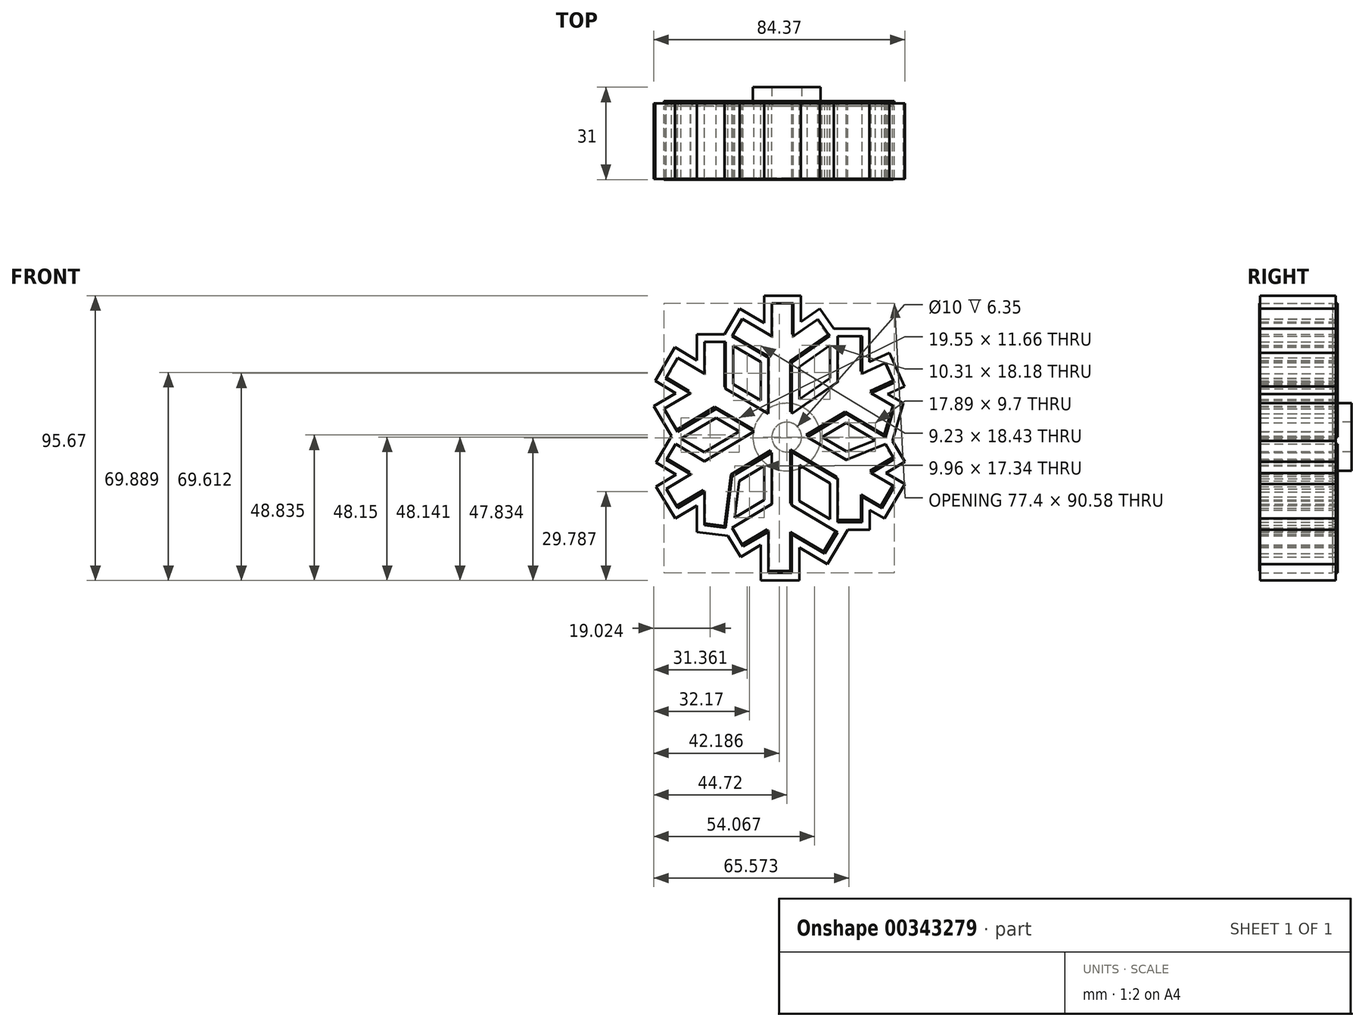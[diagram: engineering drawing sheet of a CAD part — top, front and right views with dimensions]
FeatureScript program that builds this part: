
annotation { "Feature Type Name" : "Feature", "Feature Type Description" : "" }
export const myFeature = defineFeature(function(context is Context, id is Id, definition is map)
    precondition{}
    {
        {
            var Q0;
            Q0=qCreatedBy(makeId("Front.planeOp"),FACE);
            var sketch = newSketch(context, id + "F0", { "sketchPlane" : qUnion([Q0])});
            skLineSegment(sketch, "E0", {"start": v(-40.72, 19.73) * mm, "end": v(-36.61, 26.67) * mm});
            skLineSegment(sketch, "E1", {"start": v(-36.61, 26.67) * mm, "end": v(-27.63, 21.36) * mm});
            skLineSegment(sketch, "E2", {"start": v(-27.63, 21.36) * mm, "end": v(-27.63, 32.04) * mm});
            skLineSegment(sketch, "E3", {"start": v(-27.63, 32.04) * mm, "end": v(-20.52, 32.04) * mm});
            skLineSegment(sketch, "E4", {"start": v(-20.52, 32.04) * mm, "end": v(-20.52, 16.25) * mm});
            skLineSegment(sketch, "E5", {"start": v(-20.52, 16.25) * mm, "end": v(-6.2, 7.8) * mm});
            skLineSegment(sketch, "E6", {"start": v(-6.2, 7.8) * mm, "end": v(-6.2, 21.36) * mm});
            skLineSegment(sketch, "E7", {"start": v(-6.2, 21.36) * mm, "end": v(-6.2, 26.67) * mm});
            skLineSegment(sketch, "E8", {"start": v(-6.2, 26.67) * mm, "end": v(-18.4, 33.87) * mm});
            skLineSegment(sketch, "E9", {"start": v(-18.4, 33.87) * mm, "end": v(-14.94, 39.73) * mm});
            skLineSegment(sketch, "E10", {"start": v(-14.94, 39.73) * mm, "end": v(-5.03, 33.87) * mm});
            skLineSegment(sketch, "E11", {"start": v(-5.03, 33.87) * mm, "end": v(-5.03, 44.98) * mm});
            skLineSegment(sketch, "E12", {"start": v(-5.03, 44.98) * mm, "end": v(2.2, 44.98) * mm});
            skLineSegment(sketch, "E13", {"start": v(2.2, 44.98) * mm, "end": v(2.2, 33.87) * mm});
            skLineSegment(sketch, "E14", {"start": v(2.2, 33.87) * mm, "end": v(10.42, 39.61) * mm});
            skLineSegment(sketch, "E15", {"start": v(10.42, 39.61) * mm, "end": v(14.42, 33.87) * mm});
            skLineSegment(sketch, "E16", {"start": v(14.42, 33.87) * mm, "end": v(1.65, 24.95) * mm});
            skLineSegment(sketch, "E17", {"start": v(1.65, 24.95) * mm, "end": v(1.65, 7.8) * mm});
            skLineSegment(sketch, "E18", {"start": v(1.65, 7.8) * mm, "end": v(17.04, 18.46) * mm});
            skLineSegment(sketch, "E19", {"start": v(17.04, 18.46) * mm, "end": v(17.04, 33.87) * mm});
            skLineSegment(sketch, "E20", {"start": v(17.04, 33.87) * mm, "end": v(25.25, 33.87) * mm});
            skLineSegment(sketch, "E21", {"start": v(25.25, 33.87) * mm, "end": v(25.25, 21.36) * mm});
            skLineSegment(sketch, "E22", {"start": v(25.25, 21.36) * mm, "end": v(33.14, 24.95) * mm});
            skLineSegment(sketch, "E23", {"start": v(33.14, 24.95) * mm, "end": v(36.17, 18.29) * mm});
            skLineSegment(sketch, "E24", {"start": v(36.17, 18.29) * mm, "end": v(28.4, 14.76) * mm});
            skLineSegment(sketch, "E25", {"start": v(28.4, 14.76) * mm, "end": v(36.17, 10.17) * mm});
            skLineSegment(sketch, "E26", {"start": v(36.17, 10.17) * mm, "end": v(33.14, 0) * mm});
            skLineSegment(sketch, "E27", {"start": v(33.14, 0) * mm, "end": v(19.95, 7.8) * mm});
            skLineSegment(sketch, "E28", {"start": v(19.95, 7.8) * mm, "end": v(6.94, 0) * mm});
            skLineSegment(sketch, "E29", {"start": v(6.94, 0) * mm, "end": v(19.95, -7.68) * mm});
            skLineSegment(sketch, "E30", {"start": v(19.95, -7.68) * mm, "end": v(33.14, -2.37) * mm});
            skLineSegment(sketch, "E31", {"start": v(33.14, -2.37) * mm, "end": v(36.17, -7.41) * mm});
            skLineSegment(sketch, "E32", {"start": v(36.17, -7.41) * mm, "end": v(28.4, -12.07) * mm});
            skLineSegment(sketch, "E33", {"start": v(28.4, -12.07) * mm, "end": v(36.17, -16.66) * mm});
            skLineSegment(sketch, "E34", {"start": v(36.17, -16.66) * mm, "end": v(31.88, -23.9) * mm});
            skLineSegment(sketch, "E35", {"start": v(31.88, -23.9) * mm, "end": v(25.32, -20.02) * mm});
            skLineSegment(sketch, "E36", {"start": v(25.32, -20.02) * mm, "end": v(25.32, -28.56) * mm});
            skLineSegment(sketch, "E37", {"start": v(25.32, -28.56) * mm, "end": v(17.04, -28.56) * mm});
            skLineSegment(sketch, "E38", {"start": v(17.04, -28.56) * mm, "end": v(17.04, -14.05) * mm});
            skLineSegment(sketch, "E39", {"start": v(17.04, -14.05) * mm, "end": v(1.65, -4.95) * mm});
            skLineSegment(sketch, "E40", {"start": v(1.65, -4.95) * mm, "end": v(1.65, -22.88) * mm});
            skLineSegment(sketch, "E41", {"start": v(1.65, -22.88) * mm, "end": v(17.04, -31.98) * mm});
            skLineSegment(sketch, "E42", {"start": v(17.04, -31.98) * mm, "end": v(12.78, -39.19) * mm});
            skLineSegment(sketch, "E43", {"start": v(12.78, -39.19) * mm, "end": v(1.65, -32.6) * mm});
            skLineSegment(sketch, "E44", {"start": v(1.65, -32.6) * mm, "end": v(1.65, -45.6) * mm});
            skLineSegment(sketch, "E45", {"start": v(1.65, -45.6) * mm, "end": v(-6.2, -45.6) * mm});
            skLineSegment(sketch, "E46", {"start": v(-6.2, -45.6) * mm, "end": v(-6.2, -31.72) * mm});
            skLineSegment(sketch, "E47", {"start": v(-6.2, -31.72) * mm, "end": v(-14.64, -36.78) * mm});
            skLineSegment(sketch, "E48", {"start": v(-14.64, -36.78) * mm, "end": v(-18.4, -30.51) * mm});
            skLineSegment(sketch, "E49", {"start": v(-18.4, -30.51) * mm, "end": v(-5.03, -22.5) * mm});
            skLineSegment(sketch, "E50", {"start": v(-5.03, -22.5) * mm, "end": v(-5.03, -5.2) * mm});
            skLineSegment(sketch, "E51", {"start": v(-5.03, -5.2) * mm, "end": v(-18.4, -13.22) * mm});
            skLineSegment(sketch, "E52", {"start": v(-18.4, -13.22) * mm, "end": v(-20.52, -30.51) * mm});
            skLineSegment(sketch, "E53", {"start": v(-20.52, -30.51) * mm, "end": v(-27.63, -29.64) * mm});
            skLineSegment(sketch, "E54", {"start": v(-27.63, -29.64) * mm, "end": v(-27.63, -18.46) * mm});
            skLineSegment(sketch, "E55", {"start": v(-27.63, -18.46) * mm, "end": v(-36.61, -23.85) * mm});
            skLineSegment(sketch, "E56", {"start": v(-36.61, -23.85) * mm, "end": v(-40.44, -17.48) * mm});
            skLineSegment(sketch, "E57", {"start": v(-40.44, -17.48) * mm, "end": v(-32.16, -12.52) * mm});
            skLineSegment(sketch, "E58", {"start": v(-32.16, -12.52) * mm, "end": v(-40.44, -7.63) * mm});
            skLineSegment(sketch, "E59", {"start": v(-40.44, -7.63) * mm, "end": v(-37.33, -2.37) * mm});
            skLineSegment(sketch, "E60", {"start": v(-37.33, -2.37) * mm, "end": v(-27.63, -8.1) * mm});
            skLineSegment(sketch, "E61", {"start": v(-27.63, -8.1) * mm, "end": v(-10.95, 1.9) * mm});
            skLineSegment(sketch, "E62", {"start": v(-10.95, 1.9) * mm, "end": v(-20.94, 7.8) * mm});
            skLineSegment(sketch, "E63", {"start": v(-20.94, 7.8) * mm, "end": v(-23.76, 9.47) * mm});
            skLineSegment(sketch, "E64", {"start": v(-23.76, 9.47) * mm, "end": v(-36.61, 1.76) * mm});
            skLineSegment(sketch, "E65", {"start": v(-36.61, 1.76) * mm, "end": v(-41.23, 9.47) * mm});
            skLineSegment(sketch, "E66", {"start": v(-41.23, 9.47) * mm, "end": v(-32.4, 14.76) * mm});
            skLineSegment(sketch, "E67", {"start": v(-32.4, 14.76) * mm, "end": v(-40.72, 19.73) * mm});
            skSolve(sketch);
        }
        {
            var Q0;
            Q0 = qSketchRegion(id + "F0", true);
            extrude(context, id + "F1", {"entities" : qUnion([Q0]), "depth" : .75 * mm});
        }
        {
            var Q0;
            Q0=makeQuery(id+"F1.opExtrude","CAP_FACE",FACE,{"disambiguationData":[OSD([sQuery(id+"F0.wireOp",EDGE,"E0"),sQuery(id+"F0.wireOp",EDGE,"E1"),sQuery(id+"F0.wireOp",EDGE,"E2"),sQuery(id+"F0.wireOp",EDGE,"E3"),sQuery(id+"F0.wireOp",EDGE,"E4"),sQuery(id+"F0.wireOp",EDGE,"E5"),sQuery(id+"F0.wireOp",EDGE,"E6"),sQuery(id+"F0.wireOp",EDGE,"E7"),sQuery(id+"F0.wireOp",EDGE,"E8"),sQuery(id+"F0.wireOp",EDGE,"E9"),sQuery(id+"F0.wireOp",EDGE,"E10"),sQuery(id+"F0.wireOp",EDGE,"E11"),sQuery(id+"F0.wireOp",EDGE,"E12"),sQuery(id+"F0.wireOp",EDGE,"E13"),sQuery(id+"F0.wireOp",EDGE,"E14"),sQuery(id+"F0.wireOp",EDGE,"E15"),sQuery(id+"F0.wireOp",EDGE,"E16"),sQuery(id+"F0.wireOp",EDGE,"E17"),sQuery(id+"F0.wireOp",EDGE,"E18"),sQuery(id+"F0.wireOp",EDGE,"E19"),sQuery(id+"F0.wireOp",EDGE,"E20"),sQuery(id+"F0.wireOp",EDGE,"E21"),sQuery(id+"F0.wireOp",EDGE,"E22"),sQuery(id+"F0.wireOp",EDGE,"E23"),sQuery(id+"F0.wireOp",EDGE,"E24"),sQuery(id+"F0.wireOp",EDGE,"E25"),sQuery(id+"F0.wireOp",EDGE,"E26"),sQuery(id+"F0.wireOp",EDGE,"E27"),sQuery(id+"F0.wireOp",EDGE,"E28"),sQuery(id+"F0.wireOp",EDGE,"E29"),sQuery(id+"F0.wireOp",EDGE,"E30"),sQuery(id+"F0.wireOp",EDGE,"E31"),sQuery(id+"F0.wireOp",EDGE,"E32"),sQuery(id+"F0.wireOp",EDGE,"E33"),sQuery(id+"F0.wireOp",EDGE,"E34"),sQuery(id+"F0.wireOp",EDGE,"E35"),sQuery(id+"F0.wireOp",EDGE,"E36"),sQuery(id+"F0.wireOp",EDGE,"E37"),sQuery(id+"F0.wireOp",EDGE,"E38"),sQuery(id+"F0.wireOp",EDGE,"E39"),sQuery(id+"F0.wireOp",EDGE,"E40"),sQuery(id+"F0.wireOp",EDGE,"E41"),sQuery(id+"F0.wireOp",EDGE,"E42"),sQuery(id+"F0.wireOp",EDGE,"E43"),sQuery(id+"F0.wireOp",EDGE,"E44"),sQuery(id+"F0.wireOp",EDGE,"E45"),sQuery(id+"F0.wireOp",EDGE,"E46"),sQuery(id+"F0.wireOp",EDGE,"E47"),sQuery(id+"F0.wireOp",EDGE,"E48"),sQuery(id+"F0.wireOp",EDGE,"E49"),sQuery(id+"F0.wireOp",EDGE,"E50"),sQuery(id+"F0.wireOp",EDGE,"E51"),sQuery(id+"F0.wireOp",EDGE,"E52"),sQuery(id+"F0.wireOp",EDGE,"E53"),sQuery(id+"F0.wireOp",EDGE,"E54"),sQuery(id+"F0.wireOp",EDGE,"E55"),sQuery(id+"F0.wireOp",EDGE,"E56"),sQuery(id+"F0.wireOp",EDGE,"E57"),sQuery(id+"F0.wireOp",EDGE,"E58"),sQuery(id+"F0.wireOp",EDGE,"E59"),sQuery(id+"F0.wireOp",EDGE,"E60"),sQuery(id+"F0.wireOp",EDGE,"E61"),sQuery(id+"F0.wireOp",EDGE,"E62"),sQuery(id+"F0.wireOp",EDGE,"E63"),sQuery(id+"F0.wireOp",EDGE,"E64"),sQuery(id+"F0.wireOp",EDGE,"E65"),sQuery(id+"F0.wireOp",EDGE,"E66"),sQuery(id+"F0.wireOp",EDGE,"E67")])],"isStart":false});
            var sketch = newSketch(context, id + "F2", { "sketchPlane" : qUnion([Q0])});
            skLineSegment(sketch, "E68.0", {"start": v(-8.74, 25.22) * mm, "end": v(-8.74, 12.25) * mm});
            skLineSegment(sketch, "E68.1", {"start": v(-17.98, 30.68) * mm, "end": v(-8.74, 25.22) * mm});
            skLineSegment(sketch, "E68.2", {"start": v(19.95, 4.84) * mm, "end": v(29.8, -0.98) * mm});
            skLineSegment(sketch, "E68.3", {"start": v(14.5, -15.5) * mm, "end": v(14.5, -27.53) * mm});
            skLineSegment(sketch, "E68.4", {"start": v(4.19, -9.4) * mm, "end": v(14.5, -15.5) * mm});
            skLineSegment(sketch, "E68.5", {"start": v(4.19, -21.43) * mm, "end": v(4.19, -9.4) * mm});
            skLineSegment(sketch, "E68.6", {"start": v(14.5, -27.53) * mm, "end": v(4.19, -21.43) * mm});
            skLineSegment(sketch, "E68.7", {"start": v(-8.74, 12.25) * mm, "end": v(-17.98, 17.7) * mm});
            skLineSegment(sketch, "E68.8", {"start": v(-7.57, -21.06) * mm, "end": v(-17.53, -27.03) * mm});
            skLineSegment(sketch, "E68.9", {"start": v(-7.57, -9.7) * mm, "end": v(-7.57, -21.06) * mm});
            skLineSegment(sketch, "E68.10", {"start": v(-16.03, -14.76) * mm, "end": v(-7.57, -9.7) * mm});
            skLineSegment(sketch, "E68.11", {"start": v(-17.53, -27.03) * mm, "end": v(-16.03, -14.76) * mm});
            skLineSegment(sketch, "E68.12", {"start": v(33.36, -12.05) * mm, "end": v(39.65, -8.28) * mm});
            skLineSegment(sketch, "E68.13", {"start": v(39.64, -15.77) * mm, "end": v(33.36, -12.05) * mm});
            skLineSegment(sketch, "E68.14", {"start": v(32.78, -27.38) * mm, "end": v(39.64, -15.77) * mm});
            skLineSegment(sketch, "E68.15", {"start": v(27.86, -24.48) * mm, "end": v(32.78, -27.38) * mm});
            skLineSegment(sketch, "E68.16", {"start": v(27.86, -31.1) * mm, "end": v(27.86, -24.48) * mm});
            skLineSegment(sketch, "E68.17", {"start": v(20.51, -31.1) * mm, "end": v(27.86, -31.1) * mm});
            skLineSegment(sketch, "E68.18", {"start": v(-17.98, 17.7) * mm, "end": v(-17.98, 30.68) * mm});
            skLineSegment(sketch, "E68.19", {"start": v(13.68, -42.67) * mm, "end": v(20.51, -31.1) * mm});
            skLineSegment(sketch, "E68.20", {"start": v(4.19, -37.06) * mm, "end": v(13.68, -42.67) * mm});
            skLineSegment(sketch, "E68.21", {"start": v(4.19, -48.15) * mm, "end": v(4.19, -37.06) * mm});
            skLineSegment(sketch, "E68.22", {"start": v(-8.74, -48.15) * mm, "end": v(4.19, -48.15) * mm});
            skLineSegment(sketch, "E68.23", {"start": v(-8.74, -36.2) * mm, "end": v(-8.74, -48.15) * mm});
            skLineSegment(sketch, "E68.24", {"start": v(-15.51, -40.26) * mm, "end": v(-8.74, -36.2) * mm});
            skLineSegment(sketch, "E68.25", {"start": v(-43.91, -8.52) * mm, "end": v(-37.13, -12.53) * mm});
            skLineSegment(sketch, "E68.26", {"start": v(-38.7, 0.3) * mm, "end": v(-43.91, -8.52) * mm});
            skLineSegment(sketch, "E68.27", {"start": v(-44.72, 10.34) * mm, "end": v(-38.7, 0.3) * mm});
            skLineSegment(sketch, "E68.28", {"start": v(-37.35, 14.76) * mm, "end": v(-44.72, 10.34) * mm});
            skLineSegment(sketch, "E68.29", {"start": v(-37.13, -12.53) * mm, "end": v(-43.92, -16.6) * mm});
            skLineSegment(sketch, "E68.30", {"start": v(-43.92, -16.6) * mm, "end": v(-37.48, -27.34) * mm});
            skLineSegment(sketch, "E68.31", {"start": v(14.5, 30.83) * mm, "end": v(14.5, 19.8) * mm});
            skLineSegment(sketch, "E68.32", {"start": v(-37.48, -27.34) * mm, "end": v(-30.17, -22.95) * mm});
            skLineSegment(sketch, "E68.33", {"start": v(14.5, 19.8) * mm, "end": v(4.19, 12.65) * mm});
            skLineSegment(sketch, "E68.34", {"start": v(-30.17, -22.95) * mm, "end": v(-30.17, -31.9) * mm});
            skLineSegment(sketch, "E68.35", {"start": v(-19.77, -33.17) * mm, "end": v(-15.51, -40.26) * mm});
            skLineSegment(sketch, "E68.36", {"start": v(39.65, -8.28) * mm, "end": v(35.42, -1.23) * mm});
            skLineSegment(sketch, "E68.37", {"start": v(35.42, -1.23) * mm, "end": v(39.17, 11.35) * mm});
            skLineSegment(sketch, "E68.38", {"start": v(29.8, -0.98) * mm, "end": v(20.16, -4.86) * mm});
            skLineSegment(sketch, "E68.39", {"start": v(39.17, 11.35) * mm, "end": v(33.89, 14.46) * mm});
            skLineSegment(sketch, "E68.40", {"start": v(20.16, -4.86) * mm, "end": v(11.9, 0.02) * mm});
            skLineSegment(sketch, "E68.41", {"start": v(33.89, 14.46) * mm, "end": v(39.53, 17.03) * mm});
            skLineSegment(sketch, "E68.42", {"start": v(11.9, 0.02) * mm, "end": v(19.95, 4.84) * mm});
            skLineSegment(sketch, "E68.43", {"start": v(39.53, 17.03) * mm, "end": v(34.4, 28.3) * mm});
            skLineSegment(sketch, "E68.44", {"start": v(34.4, 28.3) * mm, "end": v(27.79, 25.3) * mm});
            skLineSegment(sketch, "E68.45", {"start": v(27.79, 25.3) * mm, "end": v(27.79, 36.41) * mm});
            skLineSegment(sketch, "E68.46", {"start": v(27.79, 36.41) * mm, "end": v(15.75, 36.41) * mm});
            skLineSegment(sketch, "E68.47", {"start": v(-44.19, 18.84) * mm, "end": v(-37.35, 14.76) * mm});
            skLineSegment(sketch, "E68.48", {"start": v(15.75, 36.41) * mm, "end": v(11.04, 43.15) * mm});
            skLineSegment(sketch, "E68.49", {"start": v(11.04, 43.15) * mm, "end": v(4.75, 38.75) * mm});
            skLineSegment(sketch, "E68.50", {"start": v(4.75, 38.75) * mm, "end": v(4.75, 47.52) * mm});
            skLineSegment(sketch, "E68.51", {"start": v(4.19, 23.62) * mm, "end": v(14.5, 30.83) * mm});
            skLineSegment(sketch, "E68.52", {"start": v(4.75, 47.52) * mm, "end": v(-7.57, 47.52) * mm});
            skLineSegment(sketch, "E68.53", {"start": v(4.19, 12.65) * mm, "end": v(4.19, 23.62) * mm});
            skLineSegment(sketch, "E68.54", {"start": v(-30.17, -31.9) * mm, "end": v(-19.77, -33.17) * mm});
            skLineSegment(sketch, "E68.55", {"start": v(-27.64, -5.14) * mm, "end": v(-35.47, -0.51) * mm});
            skLineSegment(sketch, "E68.56", {"start": v(-7.57, 47.52) * mm, "end": v(-7.57, 38.33) * mm});
            skLineSegment(sketch, "E68.57", {"start": v(-7.57, 38.33) * mm, "end": v(-15.83, 43.2) * mm});
            skLineSegment(sketch, "E68.58", {"start": v(-15.83, 43.2) * mm, "end": v(-20.93, 34.58) * mm});
            skLineSegment(sketch, "E68.59", {"start": v(-20.93, 34.58) * mm, "end": v(-30.17, 34.58) * mm});
            skLineSegment(sketch, "E68.60", {"start": v(-30.17, 34.58) * mm, "end": v(-30.17, 25.81) * mm});
            skLineSegment(sketch, "E68.61", {"start": v(-30.17, 25.81) * mm, "end": v(-37.5, 30.15) * mm});
            skLineSegment(sketch, "E68.62", {"start": v(-37.5, 30.15) * mm, "end": v(-44.19, 18.84) * mm});
            skLineSegment(sketch, "E68.63", {"start": v(-35.47, -0.51) * mm, "end": v(-23.76, 6.51) * mm});
            skLineSegment(sketch, "E68.64", {"start": v(-23.76, 6.51) * mm, "end": v(-15.92, 1.88) * mm});
            skLineSegment(sketch, "E68.65", {"start": v(-15.92, 1.88) * mm, "end": v(-27.64, -5.14) * mm});
            skLineSegment(sketch, "E69.0", {"start": v(-40.37, 19.81) * mm, "end": v(-31.92, 14.76) * mm});
            skLineSegment(sketch, "E69.1", {"start": v(-36.52, 26.32) * mm, "end": v(-40.37, 19.81) * mm});
            skLineSegment(sketch, "E69.2", {"start": v(-27.37, 20.92) * mm, "end": v(-36.52, 26.32) * mm});
            skLineSegment(sketch, "E69.3", {"start": v(-27.37, 31.78) * mm, "end": v(-27.37, 20.92) * mm});
            skLineSegment(sketch, "E69.4", {"start": v(-20.77, 31.78) * mm, "end": v(-27.37, 31.78) * mm});
            skLineSegment(sketch, "E69.5", {"start": v(-20.77, 16.1) * mm, "end": v(-20.77, 31.78) * mm});
            skLineSegment(sketch, "E69.6", {"start": v(-5.95, 7.35) * mm, "end": v(-20.77, 16.1) * mm});
            skLineSegment(sketch, "E69.7", {"start": v(-5.95, 26.81) * mm, "end": v(-5.95, 7.35) * mm});
            skLineSegment(sketch, "E69.8", {"start": v(-18.05, 33.96) * mm, "end": v(-5.95, 26.81) * mm});
            skLineSegment(sketch, "E69.9", {"start": v(-14.85, 39.38) * mm, "end": v(-18.05, 33.96) * mm});
            skLineSegment(sketch, "E69.10", {"start": v(-4.78, 33.43) * mm, "end": v(-14.85, 39.38) * mm});
            skLineSegment(sketch, "E69.11", {"start": v(-4.78, 44.72) * mm, "end": v(-4.78, 33.43) * mm});
            skLineSegment(sketch, "E69.12", {"start": v(1.96, 44.72) * mm, "end": v(-4.78, 44.72) * mm});
            skLineSegment(sketch, "E69.13", {"start": v(1.96, 33.39) * mm, "end": v(1.96, 44.72) * mm});
            skLineSegment(sketch, "E69.14", {"start": v(10.35, 39.26) * mm, "end": v(1.96, 33.39) * mm});
            skLineSegment(sketch, "E69.15", {"start": v(14.07, 33.94) * mm, "end": v(10.35, 39.26) * mm});
            skLineSegment(sketch, "E69.16", {"start": v(1.4, 25.08) * mm, "end": v(14.07, 33.94) * mm});
            skLineSegment(sketch, "E69.17", {"start": v(1.4, 7.31) * mm, "end": v(1.4, 25.08) * mm});
            skLineSegment(sketch, "E69.18", {"start": v(17.3, 18.33) * mm, "end": v(1.4, 7.31) * mm});
            skLineSegment(sketch, "E69.19", {"start": v(17.3, 33.62) * mm, "end": v(17.3, 18.33) * mm});
            skLineSegment(sketch, "E69.20", {"start": v(1.4, -45.35) * mm, "end": v(1.4, -32.16) * mm});
            skLineSegment(sketch, "E69.21", {"start": v(-5.95, -45.35) * mm, "end": v(1.4, -45.35) * mm});
            skLineSegment(sketch, "E69.22", {"start": v(-5.95, -31.27) * mm, "end": v(-5.95, -45.35) * mm});
            skLineSegment(sketch, "E69.23", {"start": v(-14.55, -36.43) * mm, "end": v(-5.95, -31.27) * mm});
            skLineSegment(sketch, "E69.24", {"start": v(-18.05, -30.6) * mm, "end": v(-14.55, -36.43) * mm});
            skLineSegment(sketch, "E69.25", {"start": v(-4.78, -22.64) * mm, "end": v(-18.05, -30.6) * mm});
            skLineSegment(sketch, "E69.26", {"start": v(-4.78, -4.76) * mm, "end": v(-4.78, -22.64) * mm});
            skLineSegment(sketch, "E69.27", {"start": v(-18.63, -13.07) * mm, "end": v(-4.78, -4.76) * mm});
            skLineSegment(sketch, "E69.28", {"start": v(-20.74, -30.23) * mm, "end": v(-18.63, -13.07) * mm});
            skLineSegment(sketch, "E69.29", {"start": v(-27.37, -29.42) * mm, "end": v(-20.74, -30.23) * mm});
            skLineSegment(sketch, "E69.30", {"start": v(-27.37, -18.02) * mm, "end": v(-27.37, -29.42) * mm});
            skLineSegment(sketch, "E69.31", {"start": v(-36.52, -23.5) * mm, "end": v(-27.37, -18.02) * mm});
            skLineSegment(sketch, "E69.32", {"start": v(-23.77, 9.76) * mm, "end": v(-10.46, 1.9) * mm});
            skLineSegment(sketch, "E69.33", {"start": v(-36.52, 2.11) * mm, "end": v(-23.77, 9.76) * mm});
            skLineSegment(sketch, "E69.34", {"start": v(-40.88, 9.38) * mm, "end": v(-36.52, 2.11) * mm});
            skLineSegment(sketch, "E69.35", {"start": v(-31.92, 14.76) * mm, "end": v(-40.88, 9.38) * mm});
            skLineSegment(sketch, "E69.36", {"start": v(-10.46, 1.9) * mm, "end": v(-27.63, -8.4) * mm});
            skLineSegment(sketch, "E69.37", {"start": v(-27.63, -8.4) * mm, "end": v(-37.24, -2.72) * mm});
            skLineSegment(sketch, "E69.38", {"start": v(-37.24, -2.72) * mm, "end": v(-40.09, -7.54) * mm});
            skLineSegment(sketch, "E69.39", {"start": v(-40.09, -7.54) * mm, "end": v(-31.67, -12.51) * mm});
            skLineSegment(sketch, "E69.40", {"start": v(-31.67, -12.51) * mm, "end": v(-40.09, -17.56) * mm});
            skLineSegment(sketch, "E69.41", {"start": v(-40.09, -17.56) * mm, "end": v(-36.52, -23.5) * mm});
            skLineSegment(sketch, "E69.42", {"start": v(1.4, -32.16) * mm, "end": v(12.7, -38.84) * mm});
            skLineSegment(sketch, "E69.43", {"start": v(12.7, -38.84) * mm, "end": v(16.7, -32.07) * mm});
            skLineSegment(sketch, "E69.44", {"start": v(16.7, -32.07) * mm, "end": v(1.4, -23.03) * mm});
            skLineSegment(sketch, "E69.45", {"start": v(1.4, -23.03) * mm, "end": v(1.4, -4.5) * mm});
            skLineSegment(sketch, "E69.46", {"start": v(1.4, -4.5) * mm, "end": v(17.3, -13.9) * mm});
            skLineSegment(sketch, "E69.47", {"start": v(17.3, -13.9) * mm, "end": v(17.3, -28.3) * mm});
            skLineSegment(sketch, "E69.48", {"start": v(17.3, -28.3) * mm, "end": v(25.06, -28.3) * mm});
            skLineSegment(sketch, "E69.49", {"start": v(25.06, -28.3) * mm, "end": v(25.06, -19.58) * mm});
            skLineSegment(sketch, "E69.50", {"start": v(25.06, -19.58) * mm, "end": v(31.8, -23.56) * mm});
            skLineSegment(sketch, "E69.51", {"start": v(31.8, -23.56) * mm, "end": v(35.82, -16.75) * mm});
            skLineSegment(sketch, "E69.52", {"start": v(35.82, -16.75) * mm, "end": v(27.9, -12.07) * mm});
            skLineSegment(sketch, "E69.53", {"start": v(27.9, -12.07) * mm, "end": v(35.82, -7.32) * mm});
            skLineSegment(sketch, "E69.54", {"start": v(35.82, -7.32) * mm, "end": v(33.03, -2.68) * mm});
            skLineSegment(sketch, "E69.55", {"start": v(33.03, -2.68) * mm, "end": v(19.92, -7.97) * mm});
            skLineSegment(sketch, "E69.56", {"start": v(19.92, -7.97) * mm, "end": v(6.45, 0) * mm});
            skLineSegment(sketch, "E69.57", {"start": v(6.45, 0) * mm, "end": v(19.94, 8.1) * mm});
            skLineSegment(sketch, "E69.58", {"start": v(19.94, 8.1) * mm, "end": v(32.99, 0.38) * mm});
            skLineSegment(sketch, "E69.59", {"start": v(32.99, 0.38) * mm, "end": v(35.87, 10.05) * mm});
            skLineSegment(sketch, "E69.60", {"start": v(35.87, 10.05) * mm, "end": v(27.85, 14.79) * mm});
            skLineSegment(sketch, "E69.61", {"start": v(27.85, 14.79) * mm, "end": v(35.83, 18.42) * mm});
            skLineSegment(sketch, "E69.62", {"start": v(35.83, 18.42) * mm, "end": v(33.01, 24.6) * mm});
            skLineSegment(sketch, "E69.63", {"start": v(33.01, 24.6) * mm, "end": v(25, 20.97) * mm});
            skLineSegment(sketch, "E69.64", {"start": v(25, 20.97) * mm, "end": v(25, 33.62) * mm});
            skLineSegment(sketch, "E69.65", {"start": v(25, 33.62) * mm, "end": v(17.3, 33.62) * mm});
            skSolve(sketch);
        }
        {
            var Q0;
            Q0=makeQuery(id+"F2.imprint","IMPRINT",FACE,{"disambiguationData":[TD([[makeQuery(id+"F2.imprint","IMPRINT",EDGE,{"derivedFrom":sQuery(id+"F2.wireOp",EDGE,"E69.0")}),1.0]])]});
            extrude(context, id + "F3", {"entities" : qUnion([Q0]), "operationType" : NewBodyOperationType.REMOVE, "oppositeDirection" : true, "depth" : 25.4 * mm});
        }
        {
            var Q0;
            Q0 = qSketchRegion(id + "F2", true);
            extrude(context, id + "F4", {"entities" : qUnion([Q0]), "operationType" : NewBodyOperationType.ADD, "depth" : 1 * mm});
        }
        {
            var Q0;
            Q0=makeQuery(id+"F4.opExtrude","CAP_FACE",FACE,{"disambiguationData":[OSD([sQuery(id+"F2.wireOp",EDGE,"E68.0"),sQuery(id+"F2.wireOp",EDGE,"E68.1"),sQuery(id+"F2.wireOp",EDGE,"E68.2"),sQuery(id+"F2.wireOp",EDGE,"E68.3"),sQuery(id+"F2.wireOp",EDGE,"E68.4"),sQuery(id+"F2.wireOp",EDGE,"E68.5"),sQuery(id+"F2.wireOp",EDGE,"E68.6"),sQuery(id+"F2.wireOp",EDGE,"E68.7"),sQuery(id+"F2.wireOp",EDGE,"E68.8"),sQuery(id+"F2.wireOp",EDGE,"E68.9"),sQuery(id+"F2.wireOp",EDGE,"E68.10"),sQuery(id+"F2.wireOp",EDGE,"E68.11"),sQuery(id+"F2.wireOp",EDGE,"E68.12"),sQuery(id+"F2.wireOp",EDGE,"E68.13"),sQuery(id+"F2.wireOp",EDGE,"E68.14"),sQuery(id+"F2.wireOp",EDGE,"E68.15"),sQuery(id+"F2.wireOp",EDGE,"E68.16"),sQuery(id+"F2.wireOp",EDGE,"E68.17"),sQuery(id+"F2.wireOp",EDGE,"E68.18"),sQuery(id+"F2.wireOp",EDGE,"E68.19"),sQuery(id+"F2.wireOp",EDGE,"E68.20"),sQuery(id+"F2.wireOp",EDGE,"E68.21"),sQuery(id+"F2.wireOp",EDGE,"E68.22"),sQuery(id+"F2.wireOp",EDGE,"E68.23"),sQuery(id+"F2.wireOp",EDGE,"E68.24"),sQuery(id+"F2.wireOp",EDGE,"E68.25"),sQuery(id+"F2.wireOp",EDGE,"E68.26"),sQuery(id+"F2.wireOp",EDGE,"E68.27"),sQuery(id+"F2.wireOp",EDGE,"E68.28"),sQuery(id+"F2.wireOp",EDGE,"E68.29"),sQuery(id+"F2.wireOp",EDGE,"E68.30"),sQuery(id+"F2.wireOp",EDGE,"E68.31"),sQuery(id+"F2.wireOp",EDGE,"E68.32"),sQuery(id+"F2.wireOp",EDGE,"E68.33"),sQuery(id+"F2.wireOp",EDGE,"E68.34"),sQuery(id+"F2.wireOp",EDGE,"E68.35"),sQuery(id+"F2.wireOp",EDGE,"E68.36"),sQuery(id+"F2.wireOp",EDGE,"E68.37"),sQuery(id+"F2.wireOp",EDGE,"E68.38"),sQuery(id+"F2.wireOp",EDGE,"E68.39"),sQuery(id+"F2.wireOp",EDGE,"E68.40"),sQuery(id+"F2.wireOp",EDGE,"E68.41"),sQuery(id+"F2.wireOp",EDGE,"E68.42"),sQuery(id+"F2.wireOp",EDGE,"E68.43"),sQuery(id+"F2.wireOp",EDGE,"E68.44"),sQuery(id+"F2.wireOp",EDGE,"E68.45"),sQuery(id+"F2.wireOp",EDGE,"E68.46"),sQuery(id+"F2.wireOp",EDGE,"E68.47"),sQuery(id+"F2.wireOp",EDGE,"E68.48"),sQuery(id+"F2.wireOp",EDGE,"E68.49"),sQuery(id+"F2.wireOp",EDGE,"E68.50"),sQuery(id+"F2.wireOp",EDGE,"E68.51"),sQuery(id+"F2.wireOp",EDGE,"E68.52"),sQuery(id+"F2.wireOp",EDGE,"E68.53"),sQuery(id+"F2.wireOp",EDGE,"E68.54"),sQuery(id+"F2.wireOp",EDGE,"E68.55"),sQuery(id+"F2.wireOp",EDGE,"E68.56"),sQuery(id+"F2.wireOp",EDGE,"E68.57"),sQuery(id+"F2.wireOp",EDGE,"E68.58"),sQuery(id+"F2.wireOp",EDGE,"E68.59"),sQuery(id+"F2.wireOp",EDGE,"E68.60"),sQuery(id+"F2.wireOp",EDGE,"E68.61"),sQuery(id+"F2.wireOp",EDGE,"E68.62"),sQuery(id+"F2.wireOp",EDGE,"E68.63"),sQuery(id+"F2.wireOp",EDGE,"E68.64"),sQuery(id+"F2.wireOp",EDGE,"E68.65"),sQuery(id+"F2.wireOp",EDGE,"E69.0"),sQuery(id+"F2.wireOp",EDGE,"E69.1"),sQuery(id+"F2.wireOp",EDGE,"E69.2"),sQuery(id+"F2.wireOp",EDGE,"E69.3"),sQuery(id+"F2.wireOp",EDGE,"E69.4"),sQuery(id+"F2.wireOp",EDGE,"E69.5"),sQuery(id+"F2.wireOp",EDGE,"E69.6"),sQuery(id+"F2.wireOp",EDGE,"E69.7"),sQuery(id+"F2.wireOp",EDGE,"E69.8"),sQuery(id+"F2.wireOp",EDGE,"E69.9"),sQuery(id+"F2.wireOp",EDGE,"E69.10"),sQuery(id+"F2.wireOp",EDGE,"E69.11"),sQuery(id+"F2.wireOp",EDGE,"E69.12"),sQuery(id+"F2.wireOp",EDGE,"E69.13"),sQuery(id+"F2.wireOp",EDGE,"E69.14"),sQuery(id+"F2.wireOp",EDGE,"E69.15"),sQuery(id+"F2.wireOp",EDGE,"E69.16"),sQuery(id+"F2.wireOp",EDGE,"E69.17"),sQuery(id+"F2.wireOp",EDGE,"E69.18"),sQuery(id+"F2.wireOp",EDGE,"E69.19"),sQuery(id+"F2.wireOp",EDGE,"E69.20"),sQuery(id+"F2.wireOp",EDGE,"E69.21"),sQuery(id+"F2.wireOp",EDGE,"E69.22"),sQuery(id+"F2.wireOp",EDGE,"E69.23"),sQuery(id+"F2.wireOp",EDGE,"E69.24"),sQuery(id+"F2.wireOp",EDGE,"E69.25"),sQuery(id+"F2.wireOp",EDGE,"E69.26"),sQuery(id+"F2.wireOp",EDGE,"E69.27"),sQuery(id+"F2.wireOp",EDGE,"E69.28"),sQuery(id+"F2.wireOp",EDGE,"E69.29"),sQuery(id+"F2.wireOp",EDGE,"E69.30"),sQuery(id+"F2.wireOp",EDGE,"E69.31"),sQuery(id+"F2.wireOp",EDGE,"E69.32"),sQuery(id+"F2.wireOp",EDGE,"E69.33"),sQuery(id+"F2.wireOp",EDGE,"E69.34"),sQuery(id+"F2.wireOp",EDGE,"E69.35"),sQuery(id+"F2.wireOp",EDGE,"E69.36"),sQuery(id+"F2.wireOp",EDGE,"E69.37"),sQuery(id+"F2.wireOp",EDGE,"E69.38"),sQuery(id+"F2.wireOp",EDGE,"E69.39"),sQuery(id+"F2.wireOp",EDGE,"E69.40"),sQuery(id+"F2.wireOp",EDGE,"E69.41"),sQuery(id+"F2.wireOp",EDGE,"E69.42"),sQuery(id+"F2.wireOp",EDGE,"E69.43"),sQuery(id+"F2.wireOp",EDGE,"E69.44"),sQuery(id+"F2.wireOp",EDGE,"E69.45"),sQuery(id+"F2.wireOp",EDGE,"E69.46"),sQuery(id+"F2.wireOp",EDGE,"E69.47"),sQuery(id+"F2.wireOp",EDGE,"E69.48"),sQuery(id+"F2.wireOp",EDGE,"E69.49"),sQuery(id+"F2.wireOp",EDGE,"E69.50"),sQuery(id+"F2.wireOp",EDGE,"E69.51"),sQuery(id+"F2.wireOp",EDGE,"E69.52"),sQuery(id+"F2.wireOp",EDGE,"E69.53"),sQuery(id+"F2.wireOp",EDGE,"E69.54"),sQuery(id+"F2.wireOp",EDGE,"E69.55"),sQuery(id+"F2.wireOp",EDGE,"E69.56"),sQuery(id+"F2.wireOp",EDGE,"E69.57"),sQuery(id+"F2.wireOp",EDGE,"E69.58"),sQuery(id+"F2.wireOp",EDGE,"E69.59"),sQuery(id+"F2.wireOp",EDGE,"E69.60"),sQuery(id+"F2.wireOp",EDGE,"E69.61"),sQuery(id+"F2.wireOp",EDGE,"E69.62"),sQuery(id+"F2.wireOp",EDGE,"E69.63"),sQuery(id+"F2.wireOp",EDGE,"E69.64"),sQuery(id+"F2.wireOp",EDGE,"E69.65")])],"isStart":true});
            extrude(context, id + "F5", {"entities" : qUnion([Q0]), "operationType" : NewBodyOperationType.ADD, "oppositeDirection" : true, "depth" : 25.4 * mm});
        }
        {
            var Q0;
            Q0=makeQuery(id+"F4.opExtrude","CAP_FACE",FACE,{"disambiguationData":[OSD([sQuery(id+"F2.wireOp",EDGE,"E68.0"),sQuery(id+"F2.wireOp",EDGE,"E68.1"),sQuery(id+"F2.wireOp",EDGE,"E68.2"),sQuery(id+"F2.wireOp",EDGE,"E68.3"),sQuery(id+"F2.wireOp",EDGE,"E68.4"),sQuery(id+"F2.wireOp",EDGE,"E68.5"),sQuery(id+"F2.wireOp",EDGE,"E68.6"),sQuery(id+"F2.wireOp",EDGE,"E68.7"),sQuery(id+"F2.wireOp",EDGE,"E68.8"),sQuery(id+"F2.wireOp",EDGE,"E68.9"),sQuery(id+"F2.wireOp",EDGE,"E68.10"),sQuery(id+"F2.wireOp",EDGE,"E68.11"),sQuery(id+"F2.wireOp",EDGE,"E68.12"),sQuery(id+"F2.wireOp",EDGE,"E68.13"),sQuery(id+"F2.wireOp",EDGE,"E68.14"),sQuery(id+"F2.wireOp",EDGE,"E68.15"),sQuery(id+"F2.wireOp",EDGE,"E68.16"),sQuery(id+"F2.wireOp",EDGE,"E68.17"),sQuery(id+"F2.wireOp",EDGE,"E68.18"),sQuery(id+"F2.wireOp",EDGE,"E68.19"),sQuery(id+"F2.wireOp",EDGE,"E68.20"),sQuery(id+"F2.wireOp",EDGE,"E68.21"),sQuery(id+"F2.wireOp",EDGE,"E68.22"),sQuery(id+"F2.wireOp",EDGE,"E68.23"),sQuery(id+"F2.wireOp",EDGE,"E68.24"),sQuery(id+"F2.wireOp",EDGE,"E68.25"),sQuery(id+"F2.wireOp",EDGE,"E68.26"),sQuery(id+"F2.wireOp",EDGE,"E68.27"),sQuery(id+"F2.wireOp",EDGE,"E68.28"),sQuery(id+"F2.wireOp",EDGE,"E68.29"),sQuery(id+"F2.wireOp",EDGE,"E68.30"),sQuery(id+"F2.wireOp",EDGE,"E68.31"),sQuery(id+"F2.wireOp",EDGE,"E68.32"),sQuery(id+"F2.wireOp",EDGE,"E68.33"),sQuery(id+"F2.wireOp",EDGE,"E68.34"),sQuery(id+"F2.wireOp",EDGE,"E68.35"),sQuery(id+"F2.wireOp",EDGE,"E68.36"),sQuery(id+"F2.wireOp",EDGE,"E68.37"),sQuery(id+"F2.wireOp",EDGE,"E68.38"),sQuery(id+"F2.wireOp",EDGE,"E68.39"),sQuery(id+"F2.wireOp",EDGE,"E68.40"),sQuery(id+"F2.wireOp",EDGE,"E68.41"),sQuery(id+"F2.wireOp",EDGE,"E68.42"),sQuery(id+"F2.wireOp",EDGE,"E68.43"),sQuery(id+"F2.wireOp",EDGE,"E68.44"),sQuery(id+"F2.wireOp",EDGE,"E68.45"),sQuery(id+"F2.wireOp",EDGE,"E68.46"),sQuery(id+"F2.wireOp",EDGE,"E68.47"),sQuery(id+"F2.wireOp",EDGE,"E68.48"),sQuery(id+"F2.wireOp",EDGE,"E68.49"),sQuery(id+"F2.wireOp",EDGE,"E68.50"),sQuery(id+"F2.wireOp",EDGE,"E68.51"),sQuery(id+"F2.wireOp",EDGE,"E68.52"),sQuery(id+"F2.wireOp",EDGE,"E68.53"),sQuery(id+"F2.wireOp",EDGE,"E68.54"),sQuery(id+"F2.wireOp",EDGE,"E68.55"),sQuery(id+"F2.wireOp",EDGE,"E68.56"),sQuery(id+"F2.wireOp",EDGE,"E68.57"),sQuery(id+"F2.wireOp",EDGE,"E68.58"),sQuery(id+"F2.wireOp",EDGE,"E68.59"),sQuery(id+"F2.wireOp",EDGE,"E68.60"),sQuery(id+"F2.wireOp",EDGE,"E68.61"),sQuery(id+"F2.wireOp",EDGE,"E68.62"),sQuery(id+"F2.wireOp",EDGE,"E68.63"),sQuery(id+"F2.wireOp",EDGE,"E68.64"),sQuery(id+"F2.wireOp",EDGE,"E68.65"),sQuery(id+"F2.wireOp",EDGE,"E69.0"),sQuery(id+"F2.wireOp",EDGE,"E69.1"),sQuery(id+"F2.wireOp",EDGE,"E69.2"),sQuery(id+"F2.wireOp",EDGE,"E69.3"),sQuery(id+"F2.wireOp",EDGE,"E69.4"),sQuery(id+"F2.wireOp",EDGE,"E69.5"),sQuery(id+"F2.wireOp",EDGE,"E69.6"),sQuery(id+"F2.wireOp",EDGE,"E69.7"),sQuery(id+"F2.wireOp",EDGE,"E69.8"),sQuery(id+"F2.wireOp",EDGE,"E69.9"),sQuery(id+"F2.wireOp",EDGE,"E69.10"),sQuery(id+"F2.wireOp",EDGE,"E69.11"),sQuery(id+"F2.wireOp",EDGE,"E69.12"),sQuery(id+"F2.wireOp",EDGE,"E69.13"),sQuery(id+"F2.wireOp",EDGE,"E69.14"),sQuery(id+"F2.wireOp",EDGE,"E69.15"),sQuery(id+"F2.wireOp",EDGE,"E69.16"),sQuery(id+"F2.wireOp",EDGE,"E69.17"),sQuery(id+"F2.wireOp",EDGE,"E69.18"),sQuery(id+"F2.wireOp",EDGE,"E69.19"),sQuery(id+"F2.wireOp",EDGE,"E69.20"),sQuery(id+"F2.wireOp",EDGE,"E69.21"),sQuery(id+"F2.wireOp",EDGE,"E69.22"),sQuery(id+"F2.wireOp",EDGE,"E69.23"),sQuery(id+"F2.wireOp",EDGE,"E69.24"),sQuery(id+"F2.wireOp",EDGE,"E69.25"),sQuery(id+"F2.wireOp",EDGE,"E69.26"),sQuery(id+"F2.wireOp",EDGE,"E69.27"),sQuery(id+"F2.wireOp",EDGE,"E69.28"),sQuery(id+"F2.wireOp",EDGE,"E69.29"),sQuery(id+"F2.wireOp",EDGE,"E69.30"),sQuery(id+"F2.wireOp",EDGE,"E69.31"),sQuery(id+"F2.wireOp",EDGE,"E69.32"),sQuery(id+"F2.wireOp",EDGE,"E69.33"),sQuery(id+"F2.wireOp",EDGE,"E69.34"),sQuery(id+"F2.wireOp",EDGE,"E69.35"),sQuery(id+"F2.wireOp",EDGE,"E69.36"),sQuery(id+"F2.wireOp",EDGE,"E69.37"),sQuery(id+"F2.wireOp",EDGE,"E69.38"),sQuery(id+"F2.wireOp",EDGE,"E69.39"),sQuery(id+"F2.wireOp",EDGE,"E69.40"),sQuery(id+"F2.wireOp",EDGE,"E69.41"),sQuery(id+"F2.wireOp",EDGE,"E69.42"),sQuery(id+"F2.wireOp",EDGE,"E69.43"),sQuery(id+"F2.wireOp",EDGE,"E69.44"),sQuery(id+"F2.wireOp",EDGE,"E69.45"),sQuery(id+"F2.wireOp",EDGE,"E69.46"),sQuery(id+"F2.wireOp",EDGE,"E69.47"),sQuery(id+"F2.wireOp",EDGE,"E69.48"),sQuery(id+"F2.wireOp",EDGE,"E69.49"),sQuery(id+"F2.wireOp",EDGE,"E69.50"),sQuery(id+"F2.wireOp",EDGE,"E69.51"),sQuery(id+"F2.wireOp",EDGE,"E69.52"),sQuery(id+"F2.wireOp",EDGE,"E69.53"),sQuery(id+"F2.wireOp",EDGE,"E69.54"),sQuery(id+"F2.wireOp",EDGE,"E69.55"),sQuery(id+"F2.wireOp",EDGE,"E69.56"),sQuery(id+"F2.wireOp",EDGE,"E69.57"),sQuery(id+"F2.wireOp",EDGE,"E69.58"),sQuery(id+"F2.wireOp",EDGE,"E69.59"),sQuery(id+"F2.wireOp",EDGE,"E69.60"),sQuery(id+"F2.wireOp",EDGE,"E69.61"),sQuery(id+"F2.wireOp",EDGE,"E69.62"),sQuery(id+"F2.wireOp",EDGE,"E69.63"),sQuery(id+"F2.wireOp",EDGE,"E69.64"),sQuery(id+"F2.wireOp",EDGE,"E69.65")])],"isStart":false});
            var sketch = newSketch(context, id + "F6", { "sketchPlane" : qUnion([Q0])});
            skCircle(sketch, "E70", {"center": v(0, 0) * mm, "radius": 5 * mm});
            skCircle(sketch, "E71.0", {"center": v(0, 0) * mm, "radius": 11.35 * mm});
            skSolve(sketch);
        }
        {
            var Q0;
            Q0 = qSketchRegion(id + "F6", true);
            extrude(context, id + "F7", {"entities" : qUnion([Q0]), "operationType" : NewBodyOperationType.ADD, "oppositeDirection" : true, "depth" : 6.35 * mm});
        }
        {
            var Q0;
            Q0=makeQuery(id+"F5.opExtrude","CAP_FACE",FACE,{"disambiguationData":[OSD([sQuery(id+"F2.wireOp",EDGE,"E68.0"),sQuery(id+"F2.wireOp",EDGE,"E68.1"),sQuery(id+"F2.wireOp",EDGE,"E68.2"),sQuery(id+"F2.wireOp",EDGE,"E68.3"),sQuery(id+"F2.wireOp",EDGE,"E68.4"),sQuery(id+"F2.wireOp",EDGE,"E68.5"),sQuery(id+"F2.wireOp",EDGE,"E68.6"),sQuery(id+"F2.wireOp",EDGE,"E68.7"),sQuery(id+"F2.wireOp",EDGE,"E68.8"),sQuery(id+"F2.wireOp",EDGE,"E68.9"),sQuery(id+"F2.wireOp",EDGE,"E68.10"),sQuery(id+"F2.wireOp",EDGE,"E68.11"),sQuery(id+"F2.wireOp",EDGE,"E68.12"),sQuery(id+"F2.wireOp",EDGE,"E68.13"),sQuery(id+"F2.wireOp",EDGE,"E68.14"),sQuery(id+"F2.wireOp",EDGE,"E68.15"),sQuery(id+"F2.wireOp",EDGE,"E68.16"),sQuery(id+"F2.wireOp",EDGE,"E68.17"),sQuery(id+"F2.wireOp",EDGE,"E68.18"),sQuery(id+"F2.wireOp",EDGE,"E68.19"),sQuery(id+"F2.wireOp",EDGE,"E68.20"),sQuery(id+"F2.wireOp",EDGE,"E68.21"),sQuery(id+"F2.wireOp",EDGE,"E68.22"),sQuery(id+"F2.wireOp",EDGE,"E68.23"),sQuery(id+"F2.wireOp",EDGE,"E68.24"),sQuery(id+"F2.wireOp",EDGE,"E68.25"),sQuery(id+"F2.wireOp",EDGE,"E68.26"),sQuery(id+"F2.wireOp",EDGE,"E68.27"),sQuery(id+"F2.wireOp",EDGE,"E68.28"),sQuery(id+"F2.wireOp",EDGE,"E68.29"),sQuery(id+"F2.wireOp",EDGE,"E68.30"),sQuery(id+"F2.wireOp",EDGE,"E68.31"),sQuery(id+"F2.wireOp",EDGE,"E68.32"),sQuery(id+"F2.wireOp",EDGE,"E68.33"),sQuery(id+"F2.wireOp",EDGE,"E68.34"),sQuery(id+"F2.wireOp",EDGE,"E68.35"),sQuery(id+"F2.wireOp",EDGE,"E68.36"),sQuery(id+"F2.wireOp",EDGE,"E68.37"),sQuery(id+"F2.wireOp",EDGE,"E68.38"),sQuery(id+"F2.wireOp",EDGE,"E68.39"),sQuery(id+"F2.wireOp",EDGE,"E68.40"),sQuery(id+"F2.wireOp",EDGE,"E68.41"),sQuery(id+"F2.wireOp",EDGE,"E68.42"),sQuery(id+"F2.wireOp",EDGE,"E68.43"),sQuery(id+"F2.wireOp",EDGE,"E68.44"),sQuery(id+"F2.wireOp",EDGE,"E68.45"),sQuery(id+"F2.wireOp",EDGE,"E68.46"),sQuery(id+"F2.wireOp",EDGE,"E68.47"),sQuery(id+"F2.wireOp",EDGE,"E68.48"),sQuery(id+"F2.wireOp",EDGE,"E68.49"),sQuery(id+"F2.wireOp",EDGE,"E68.50"),sQuery(id+"F2.wireOp",EDGE,"E68.51"),sQuery(id+"F2.wireOp",EDGE,"E68.52"),sQuery(id+"F2.wireOp",EDGE,"E68.53"),sQuery(id+"F2.wireOp",EDGE,"E68.54"),sQuery(id+"F2.wireOp",EDGE,"E68.55"),sQuery(id+"F2.wireOp",EDGE,"E68.56"),sQuery(id+"F2.wireOp",EDGE,"E68.57"),sQuery(id+"F2.wireOp",EDGE,"E68.58"),sQuery(id+"F2.wireOp",EDGE,"E68.59"),sQuery(id+"F2.wireOp",EDGE,"E68.60"),sQuery(id+"F2.wireOp",EDGE,"E68.61"),sQuery(id+"F2.wireOp",EDGE,"E68.62"),sQuery(id+"F2.wireOp",EDGE,"E68.63"),sQuery(id+"F2.wireOp",EDGE,"E68.64"),sQuery(id+"F2.wireOp",EDGE,"E68.65"),sQuery(id+"F2.wireOp",EDGE,"E69.0"),sQuery(id+"F2.wireOp",EDGE,"E69.1"),sQuery(id+"F2.wireOp",EDGE,"E69.2"),sQuery(id+"F2.wireOp",EDGE,"E69.3"),sQuery(id+"F2.wireOp",EDGE,"E69.4"),sQuery(id+"F2.wireOp",EDGE,"E69.5"),sQuery(id+"F2.wireOp",EDGE,"E69.6"),sQuery(id+"F2.wireOp",EDGE,"E69.7"),sQuery(id+"F2.wireOp",EDGE,"E69.8"),sQuery(id+"F2.wireOp",EDGE,"E69.9"),sQuery(id+"F2.wireOp",EDGE,"E69.10"),sQuery(id+"F2.wireOp",EDGE,"E69.11"),sQuery(id+"F2.wireOp",EDGE,"E69.12"),sQuery(id+"F2.wireOp",EDGE,"E69.13"),sQuery(id+"F2.wireOp",EDGE,"E69.14"),sQuery(id+"F2.wireOp",EDGE,"E69.15"),sQuery(id+"F2.wireOp",EDGE,"E69.16"),sQuery(id+"F2.wireOp",EDGE,"E69.17"),sQuery(id+"F2.wireOp",EDGE,"E69.18"),sQuery(id+"F2.wireOp",EDGE,"E69.19"),sQuery(id+"F2.wireOp",EDGE,"E69.20"),sQuery(id+"F2.wireOp",EDGE,"E69.21"),sQuery(id+"F2.wireOp",EDGE,"E69.22"),sQuery(id+"F2.wireOp",EDGE,"E69.23"),sQuery(id+"F2.wireOp",EDGE,"E69.24"),sQuery(id+"F2.wireOp",EDGE,"E69.25"),sQuery(id+"F2.wireOp",EDGE,"E69.26"),sQuery(id+"F2.wireOp",EDGE,"E69.27"),sQuery(id+"F2.wireOp",EDGE,"E69.28"),sQuery(id+"F2.wireOp",EDGE,"E69.29"),sQuery(id+"F2.wireOp",EDGE,"E69.30"),sQuery(id+"F2.wireOp",EDGE,"E69.31"),sQuery(id+"F2.wireOp",EDGE,"E69.32"),sQuery(id+"F2.wireOp",EDGE,"E69.33"),sQuery(id+"F2.wireOp",EDGE,"E69.34"),sQuery(id+"F2.wireOp",EDGE,"E69.35"),sQuery(id+"F2.wireOp",EDGE,"E69.36"),sQuery(id+"F2.wireOp",EDGE,"E69.37"),sQuery(id+"F2.wireOp",EDGE,"E69.38"),sQuery(id+"F2.wireOp",EDGE,"E69.39"),sQuery(id+"F2.wireOp",EDGE,"E69.40"),sQuery(id+"F2.wireOp",EDGE,"E69.41"),sQuery(id+"F2.wireOp",EDGE,"E69.42"),sQuery(id+"F2.wireOp",EDGE,"E69.43"),sQuery(id+"F2.wireOp",EDGE,"E69.44"),sQuery(id+"F2.wireOp",EDGE,"E69.45"),sQuery(id+"F2.wireOp",EDGE,"E69.46"),sQuery(id+"F2.wireOp",EDGE,"E69.47"),sQuery(id+"F2.wireOp",EDGE,"E69.48"),sQuery(id+"F2.wireOp",EDGE,"E69.49"),sQuery(id+"F2.wireOp",EDGE,"E69.50"),sQuery(id+"F2.wireOp",EDGE,"E69.51"),sQuery(id+"F2.wireOp",EDGE,"E69.52"),sQuery(id+"F2.wireOp",EDGE,"E69.53"),sQuery(id+"F2.wireOp",EDGE,"E69.54"),sQuery(id+"F2.wireOp",EDGE,"E69.55"),sQuery(id+"F2.wireOp",EDGE,"E69.56"),sQuery(id+"F2.wireOp",EDGE,"E69.57"),sQuery(id+"F2.wireOp",EDGE,"E69.58"),sQuery(id+"F2.wireOp",EDGE,"E69.59"),sQuery(id+"F2.wireOp",EDGE,"E69.60"),sQuery(id+"F2.wireOp",EDGE,"E69.61"),sQuery(id+"F2.wireOp",EDGE,"E69.62"),sQuery(id+"F2.wireOp",EDGE,"E69.63"),sQuery(id+"F2.wireOp",EDGE,"E69.64"),sQuery(id+"F2.wireOp",EDGE,"E69.65")])],"isStart":false});
            var sketch = newSketch(context, id + "F8", { "sketchPlane" : qUnion([Q0])});
            skLineSegment(sketch, "E72", {"start": v(-41.13, 20.41) * mm, "end": v(-37.02, 27.35) * mm});
            skLineSegment(sketch, "E73", {"start": v(-37.02, 27.35) * mm, "end": v(-28.04, 22.04) * mm});
            skLineSegment(sketch, "E74", {"start": v(-28.04, 22.04) * mm, "end": v(-28.04, 32.72) * mm});
            skLineSegment(sketch, "E75", {"start": v(-28.04, 32.72) * mm, "end": v(-20.93, 32.72) * mm});
            skLineSegment(sketch, "E76", {"start": v(-20.93, 32.72) * mm, "end": v(-20.93, 16.94) * mm});
            skLineSegment(sketch, "E77", {"start": v(-20.93, 16.94) * mm, "end": v(-6.61, 8.48) * mm});
            skLineSegment(sketch, "E78", {"start": v(-6.61, 8.48) * mm, "end": v(-6.61, 22.04) * mm});
            skLineSegment(sketch, "E79", {"start": v(-6.61, 22.04) * mm, "end": v(-6.61, 27.35) * mm});
            skLineSegment(sketch, "E80", {"start": v(-6.61, 27.35) * mm, "end": v(-18.8, 34.56) * mm});
            skLineSegment(sketch, "E81", {"start": v(-18.8, 34.56) * mm, "end": v(-15.35, 40.41) * mm});
            skLineSegment(sketch, "E82", {"start": v(-15.35, 40.41) * mm, "end": v(-5.44, 34.56) * mm});
            skLineSegment(sketch, "E83", {"start": v(-5.44, 34.56) * mm, "end": v(-5.44, 45.66) * mm});
            skLineSegment(sketch, "E84", {"start": v(-5.44, 45.66) * mm, "end": v(1.8, 45.66) * mm});
            skLineSegment(sketch, "E85", {"start": v(1.8, 45.66) * mm, "end": v(1.8, 34.56) * mm});
            skLineSegment(sketch, "E86", {"start": v(1.8, 34.56) * mm, "end": v(10, 40.3) * mm});
            skLineSegment(sketch, "E87", {"start": v(10, 40.3) * mm, "end": v(14.01, 34.56) * mm});
            skLineSegment(sketch, "E88", {"start": v(14.01, 34.56) * mm, "end": v(1.24, 25.63) * mm});
            skLineSegment(sketch, "E89", {"start": v(1.24, 25.63) * mm, "end": v(1.24, 8.48) * mm});
            skLineSegment(sketch, "E90", {"start": v(1.24, 8.48) * mm, "end": v(16.63, 19.15) * mm});
            skLineSegment(sketch, "E91", {"start": v(16.63, 19.15) * mm, "end": v(16.63, 34.56) * mm});
            skLineSegment(sketch, "E92", {"start": v(16.63, 34.56) * mm, "end": v(24.84, 34.56) * mm});
            skLineSegment(sketch, "E93", {"start": v(24.84, 34.56) * mm, "end": v(24.84, 22.04) * mm});
            skLineSegment(sketch, "E94", {"start": v(24.84, 22.04) * mm, "end": v(32.73, 25.63) * mm});
            skLineSegment(sketch, "E95", {"start": v(32.73, 25.63) * mm, "end": v(35.75, 18.97) * mm});
            skLineSegment(sketch, "E96", {"start": v(35.75, 18.97) * mm, "end": v(27.99, 15.44) * mm});
            skLineSegment(sketch, "E97", {"start": v(27.99, 15.44) * mm, "end": v(35.75, 10.85) * mm});
            skLineSegment(sketch, "E98", {"start": v(35.75, 10.85) * mm, "end": v(32.73, 0.68) * mm});
            skLineSegment(sketch, "E99", {"start": v(32.73, 0.68) * mm, "end": v(19.54, 8.48) * mm});
            skLineSegment(sketch, "E100", {"start": v(19.54, 8.48) * mm, "end": v(6.53, 0.68) * mm});
            skLineSegment(sketch, "E101", {"start": v(6.53, 0.68) * mm, "end": v(19.54, -7) * mm});
            skLineSegment(sketch, "E102", {"start": v(19.54, -7) * mm, "end": v(32.73, -1.68) * mm});
            skLineSegment(sketch, "E103", {"start": v(32.73, -1.68) * mm, "end": v(35.75, -6.73) * mm});
            skLineSegment(sketch, "E104", {"start": v(35.75, -6.73) * mm, "end": v(27.99, -11.39) * mm});
            skLineSegment(sketch, "E105", {"start": v(27.99, -11.39) * mm, "end": v(35.75, -15.98) * mm});
            skLineSegment(sketch, "E106", {"start": v(35.75, -15.98) * mm, "end": v(31.47, -23.22) * mm});
            skLineSegment(sketch, "E107", {"start": v(31.47, -23.22) * mm, "end": v(24.9, -19.34) * mm});
            skLineSegment(sketch, "E108", {"start": v(24.9, -19.34) * mm, "end": v(24.9, -27.88) * mm});
            skLineSegment(sketch, "E109", {"start": v(24.9, -27.88) * mm, "end": v(16.63, -27.88) * mm});
            skLineSegment(sketch, "E110", {"start": v(16.63, -27.88) * mm, "end": v(16.63, -13.36) * mm});
            skLineSegment(sketch, "E111", {"start": v(16.63, -13.36) * mm, "end": v(1.24, -4.26) * mm});
            skLineSegment(sketch, "E112", {"start": v(1.24, -4.26) * mm, "end": v(1.24, -22.2) * mm});
            skLineSegment(sketch, "E113", {"start": v(1.24, -22.2) * mm, "end": v(16.63, -31.3) * mm});
            skLineSegment(sketch, "E114", {"start": v(16.63, -31.3) * mm, "end": v(12.37, -38.5) * mm});
            skLineSegment(sketch, "E115", {"start": v(12.37, -38.5) * mm, "end": v(1.24, -31.92) * mm});
            skLineSegment(sketch, "E116", {"start": v(1.24, -31.92) * mm, "end": v(1.24, -44.92) * mm});
            skLineSegment(sketch, "E117", {"start": v(1.24, -44.92) * mm, "end": v(-6.61, -44.92) * mm});
            skLineSegment(sketch, "E118", {"start": v(-6.61, -44.92) * mm, "end": v(-6.61, -31.04) * mm});
            skLineSegment(sketch, "E119", {"start": v(-6.61, -31.04) * mm, "end": v(-15.05, -36.1) * mm});
            skLineSegment(sketch, "E120", {"start": v(-15.05, -36.1) * mm, "end": v(-18.8, -29.83) * mm});
            skLineSegment(sketch, "E121", {"start": v(-18.8, -29.83) * mm, "end": v(-5.44, -21.82) * mm});
            skLineSegment(sketch, "E122", {"start": v(-5.44, -21.82) * mm, "end": v(-5.44, -4.52) * mm});
            skLineSegment(sketch, "E123", {"start": v(-5.44, -4.52) * mm, "end": v(-18.8, -12.54) * mm});
            skLineSegment(sketch, "E124", {"start": v(-18.8, -12.54) * mm, "end": v(-20.93, -29.83) * mm});
            skLineSegment(sketch, "E125", {"start": v(-20.93, -29.83) * mm, "end": v(-28.04, -28.96) * mm});
            skLineSegment(sketch, "E126", {"start": v(-28.04, -28.96) * mm, "end": v(-28.04, -17.78) * mm});
            skLineSegment(sketch, "E127", {"start": v(-28.04, -17.78) * mm, "end": v(-37.02, -23.17) * mm});
            skLineSegment(sketch, "E128", {"start": v(-37.02, -23.17) * mm, "end": v(-40.85, -16.8) * mm});
            skLineSegment(sketch, "E129", {"start": v(-40.85, -16.8) * mm, "end": v(-32.57, -11.83) * mm});
            skLineSegment(sketch, "E130", {"start": v(-32.57, -11.83) * mm, "end": v(-40.85, -6.94) * mm});
            skLineSegment(sketch, "E131", {"start": v(-40.85, -6.94) * mm, "end": v(-37.74, -1.68) * mm});
            skLineSegment(sketch, "E132", {"start": v(-37.74, -1.68) * mm, "end": v(-28.04, -7.42) * mm});
            skLineSegment(sketch, "E133", {"start": v(-28.04, -7.42) * mm, "end": v(-11.36, 2.58) * mm});
            skLineSegment(sketch, "E134", {"start": v(-11.36, 2.58) * mm, "end": v(-21.35, 8.48) * mm});
            skLineSegment(sketch, "E135", {"start": v(-21.35, 8.48) * mm, "end": v(-24.18, 10.15) * mm});
            skLineSegment(sketch, "E136", {"start": v(-24.18, 10.15) * mm, "end": v(-37.02, 2.45) * mm});
            skLineSegment(sketch, "E137", {"start": v(-37.02, 2.45) * mm, "end": v(-41.64, 10.15) * mm});
            skLineSegment(sketch, "E138", {"start": v(-41.64, 10.15) * mm, "end": v(-32.82, 15.44) * mm});
            skLineSegment(sketch, "E139", {"start": v(-32.82, 15.44) * mm, "end": v(-41.13, 20.41) * mm});
            skSolve(sketch);
        }
        {
            var Q0;
            {var subQ37=sQuery(id+"F8.wireOp",EDGE,"E89");Q0=makeQuery(id+"F8.imprint","IMPRINT",FACE,{"disambiguationData":[TD([[makeQuery(id+"F8.imprint","IMPRINT",EDGE,{"derivedFrom":subQ37}),-1.0]])]});}
            extrude(context, id + "F9", {"entities" : qUnion([Q0]), "operationType" : NewBodyOperationType.ADD, "endBound" : BoundingType.SYMMETRIC, "depth" : .5 * mm});
        }
    });
